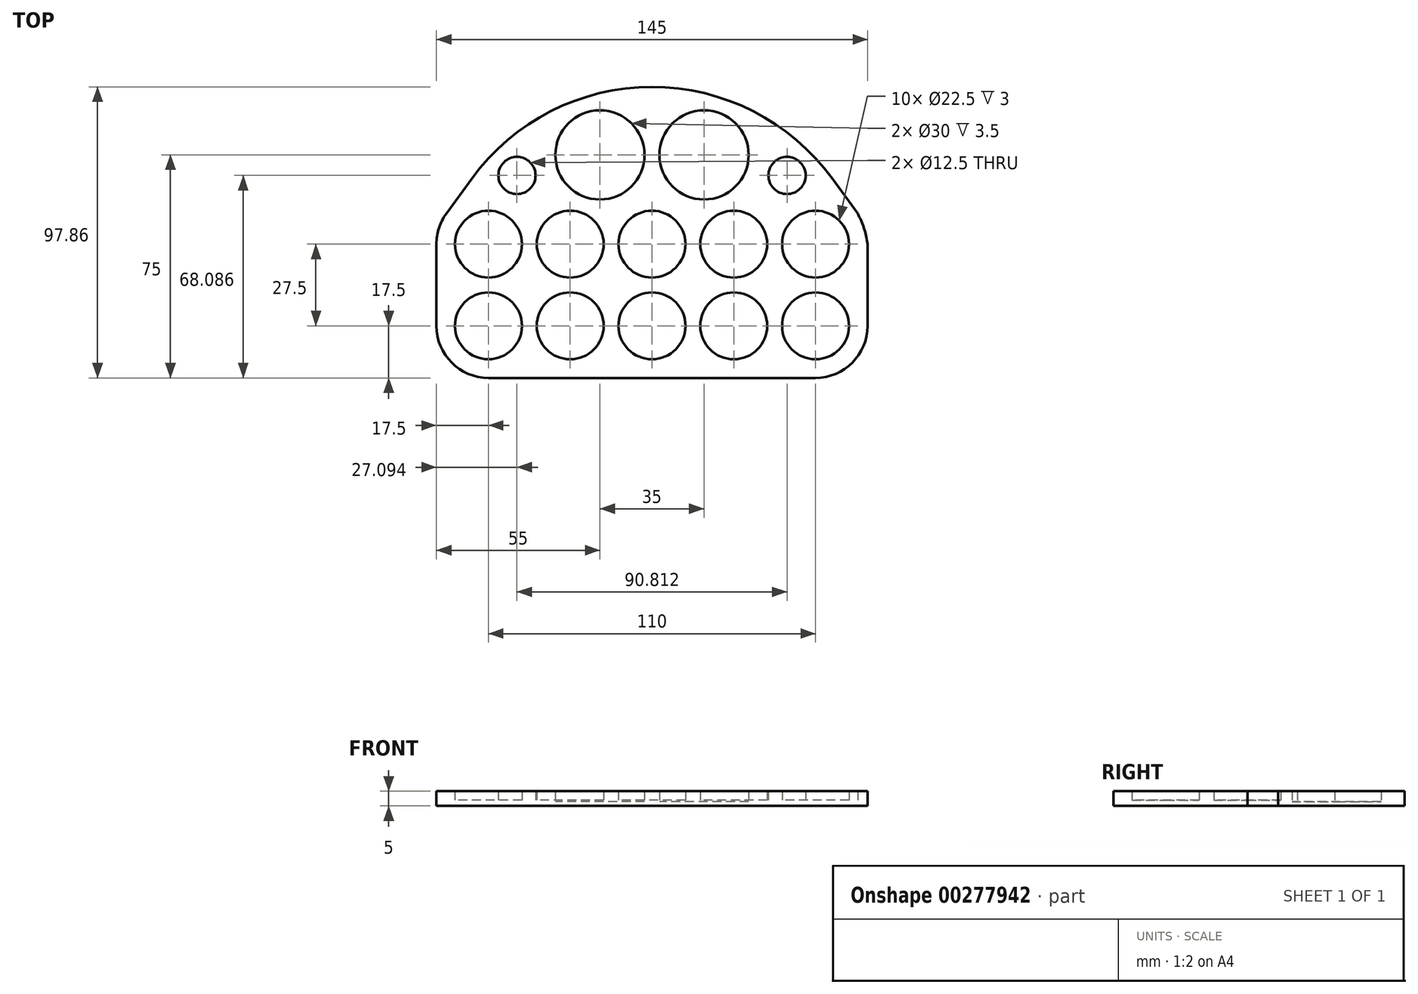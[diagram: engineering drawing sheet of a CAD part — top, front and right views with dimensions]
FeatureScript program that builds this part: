
annotation { "Feature Type Name" : "Feature", "Feature Type Description" : "" }
export const myFeature = defineFeature(function(context is Context, id is Id, definition is map)
    precondition{}
    {
        {
            var Q0;
            Q0=qCreatedBy(makeId("Top.planeOp"),FACE);
            var sketch = newSketch(context, id + "F0", { "sketchPlane" : qUnion([Q0])});
            skCircle(sketch, "E0", {"center": v(17.5, 17.5) * mm, "radius": 11.25 * mm});
            skCircle(sketch, "E1.0.1.0", {"center": v(17.5, 45) * mm, "radius": 11.25 * mm});
            skCircle(sketch, "E1.1.0.0", {"center": v(45, 17.5) * mm, "radius": 11.25 * mm});
            skCircle(sketch, "E1.1.1.0", {"center": v(45, 45) * mm, "radius": 11.25 * mm});
            skCircle(sketch, "E1.2.0.0", {"center": v(72.5, 17.5) * mm, "radius": 11.25 * mm});
            skCircle(sketch, "E1.2.1.0", {"center": v(72.5, 45) * mm, "radius": 11.25 * mm});
            skCircle(sketch, "E1.3.0.0", {"center": v(100, 17.5) * mm, "radius": 11.25 * mm});
            skCircle(sketch, "E1.3.1.0", {"center": v(100, 45) * mm, "radius": 11.25 * mm});
            skCircle(sketch, "E1.4.0.0", {"center": v(127.5, 17.5) * mm, "radius": 11.25 * mm});
            skCircle(sketch, "E1.4.1.0", {"center": v(127.5, 45) * mm, "radius": 11.25 * mm});
            skLineSegment(sketch, "E1.direction1", {"start": v(17.5, 17.5) * mm, "end": v(45, 17.5) * mm, "construction": true});
            skLineSegment(sketch, "E1.direction2", {"start": v(17.5, 17.5) * mm, "end": v(17.5, 45) * mm, "construction": true});
            skLineSegment(sketch, "E2", {"start": v(-31.67, 31.25) * mm, "end": v(207.93, 31.25) * mm, "construction": true});
            skCircle(sketch, "E3", {"center": v(55, 75) * mm, "radius": 15 * mm});
            skCircle(sketch, "E4", {"center": v(90, 75) * mm, "radius": 15 * mm});
            skLineSegment(sketch, "E5", {"start": v(72.5, 106.06) * mm, "end": v(72.5, -40.38) * mm, "construction": true});
            skLineSegment(sketch, "E6.left", {"start": v(0, 45) * mm, "end": v(0, 17.5) * mm});
            skArc(sketch, "E7", {"start": v(72.5, 97.86) * mm, "mid": v(38.47, 89.7) * mm, "end": v(11.86, 66.99) * mm});
            skLineSegment(sketch, "E8", {"start": v(3.35, 55.3) * mm, "end": v(11.86, 66.99) * mm});
            skArc(sketch, "E9", {"start": v(0, 17.5) * mm, "mid": v(5.13, 5.13) * mm, "end": v(17.5, 0) * mm});
            skLineSegment(sketch, "E10.MirrorCS", {"start": v(141.65, 55.3) * mm, "end": v(133.14, 66.99) * mm});
            skArc(sketch, "E11.MirrorCS", {"start": v(145, 45) * mm, "mid": v(143.8, 50.3) * mm, "end": v(141.65, 55.3) * mm});
            skLineSegment(sketch, "E12.MirrorCS", {"start": v(145, 45) * mm, "end": v(145, 17.5) * mm});
            skLineSegment(sketch, "E13", {"start": v(17.5, 0) * mm, "end": v(127.5, 0) * mm});
            skArc(sketch, "E14", {"start": v(3.35, 55.3) * mm, "mid": v(0.86, 50.41) * mm, "end": v(0, 45) * mm});
            skArc(sketch, "E15", {"start": v(127.5, 0) * mm, "mid": v(139.87, 5.13) * mm, "end": v(145, 17.5) * mm});
            skArc(sketch, "E16", {"start": v(133.14, 66.99) * mm, "mid": v(106.53, 89.7) * mm, "end": v(72.5, 97.86) * mm});
            skCircle(sketch, "E17", {"center": v(27.1, 68.09) * mm, "radius": 6.25 * mm});
            skCircle(sketch, "E18.MirrorC", {"center": v(117.9, 68.09) * mm, "radius": 6.25 * mm});
            skSolve(sketch);
        }
        {
            var Q0;
            Q0 = qSketchRegion(id + "F0", true);
            extrude(context, id + "F1", {"entities" : qUnion([Q0]), "depth" : 5 * mm});
        }
        {
            var Q0;
            Q0=makeQuery(id+"F0.imprint","IMPRINT",FACE,{"disambiguationData":[TD([[makeQuery(id+"F0.imprint","IMPRINT",EDGE,{"derivedFrom":sQuery(id+"F0.wireOp",EDGE,"E3")}),1.0]])]});
            var Q1;
            Q1=makeQuery(id+"F0.imprint","IMPRINT",FACE,{"disambiguationData":[TD([[makeQuery(id+"F0.imprint","IMPRINT",EDGE,{"derivedFrom":sQuery(id+"F0.wireOp",EDGE,"E4")}),1.0]])]});
            extrude(context, id + "F2", {"entities" : qUnion([Q0, Q1]), "operationType" : NewBodyOperationType.ADD, "depth" : (5 - 3.5) * mm});
        }
        {
            var Q0;
            Q0=makeQuery(id+"F0.imprint","IMPRINT",FACE,{"disambiguationData":[TD([[makeQuery(id+"F0.imprint","IMPRINT",EDGE,{"derivedFrom":sQuery(id+"F0.wireOp",EDGE,"E1.0.1.0")}),1.0]])]});
            var Q1;
            Q1=makeQuery(id+"F0.imprint","IMPRINT",FACE,{"disambiguationData":[TD([[makeQuery(id+"F0.imprint","IMPRINT",EDGE,{"derivedFrom":sQuery(id+"F0.wireOp",EDGE,"E0")}),1.0]])]});
            var Q2;
            Q2=makeQuery(id+"F0.imprint","IMPRINT",FACE,{"disambiguationData":[TD([[makeQuery(id+"F0.imprint","IMPRINT",EDGE,{"derivedFrom":sQuery(id+"F0.wireOp",EDGE,"E1.1.1.0")}),1.0]])]});
            var Q3;
            Q3=makeQuery(id+"F0.imprint","IMPRINT",FACE,{"disambiguationData":[TD([[makeQuery(id+"F0.imprint","IMPRINT",EDGE,{"derivedFrom":sQuery(id+"F0.wireOp",EDGE,"E1.1.0.0")}),1.0]])]});
            var Q4;
            Q4=makeQuery(id+"F0.imprint","IMPRINT",FACE,{"disambiguationData":[TD([[makeQuery(id+"F0.imprint","IMPRINT",EDGE,{"derivedFrom":sQuery(id+"F0.wireOp",EDGE,"E1.2.1.0")}),1.0]])]});
            var Q5;
            Q5=makeQuery(id+"F0.imprint","IMPRINT",FACE,{"disambiguationData":[TD([[makeQuery(id+"F0.imprint","IMPRINT",EDGE,{"derivedFrom":sQuery(id+"F0.wireOp",EDGE,"E1.2.0.0")}),1.0]])]});
            var Q6;
            Q6=makeQuery(id+"F0.imprint","IMPRINT",FACE,{"disambiguationData":[TD([[makeQuery(id+"F0.imprint","IMPRINT",EDGE,{"derivedFrom":sQuery(id+"F0.wireOp",EDGE,"E1.3.1.0")}),1.0]])]});
            var Q7;
            Q7=makeQuery(id+"F0.imprint","IMPRINT",FACE,{"disambiguationData":[TD([[makeQuery(id+"F0.imprint","IMPRINT",EDGE,{"derivedFrom":sQuery(id+"F0.wireOp",EDGE,"E1.3.0.0")}),1.0]])]});
            var Q8;
            Q8=makeQuery(id+"F0.imprint","IMPRINT",FACE,{"disambiguationData":[TD([[makeQuery(id+"F0.imprint","IMPRINT",EDGE,{"derivedFrom":sQuery(id+"F0.wireOp",EDGE,"E1.4.1.0")}),1.0]])]});
            var Q9;
            Q9=makeQuery(id+"F0.imprint","IMPRINT",FACE,{"disambiguationData":[TD([[makeQuery(id+"F0.imprint","IMPRINT",EDGE,{"derivedFrom":sQuery(id+"F0.wireOp",EDGE,"E1.4.0.0")}),1.0]])]});
            extrude(context, id + "F3", {"entities" : qUnion([Q0, Q1, Q2, Q3, Q4, Q5, Q6, Q7, Q8, Q9]), "operationType" : NewBodyOperationType.ADD, "depth" : (5 - 3) * mm});
        }
    });
